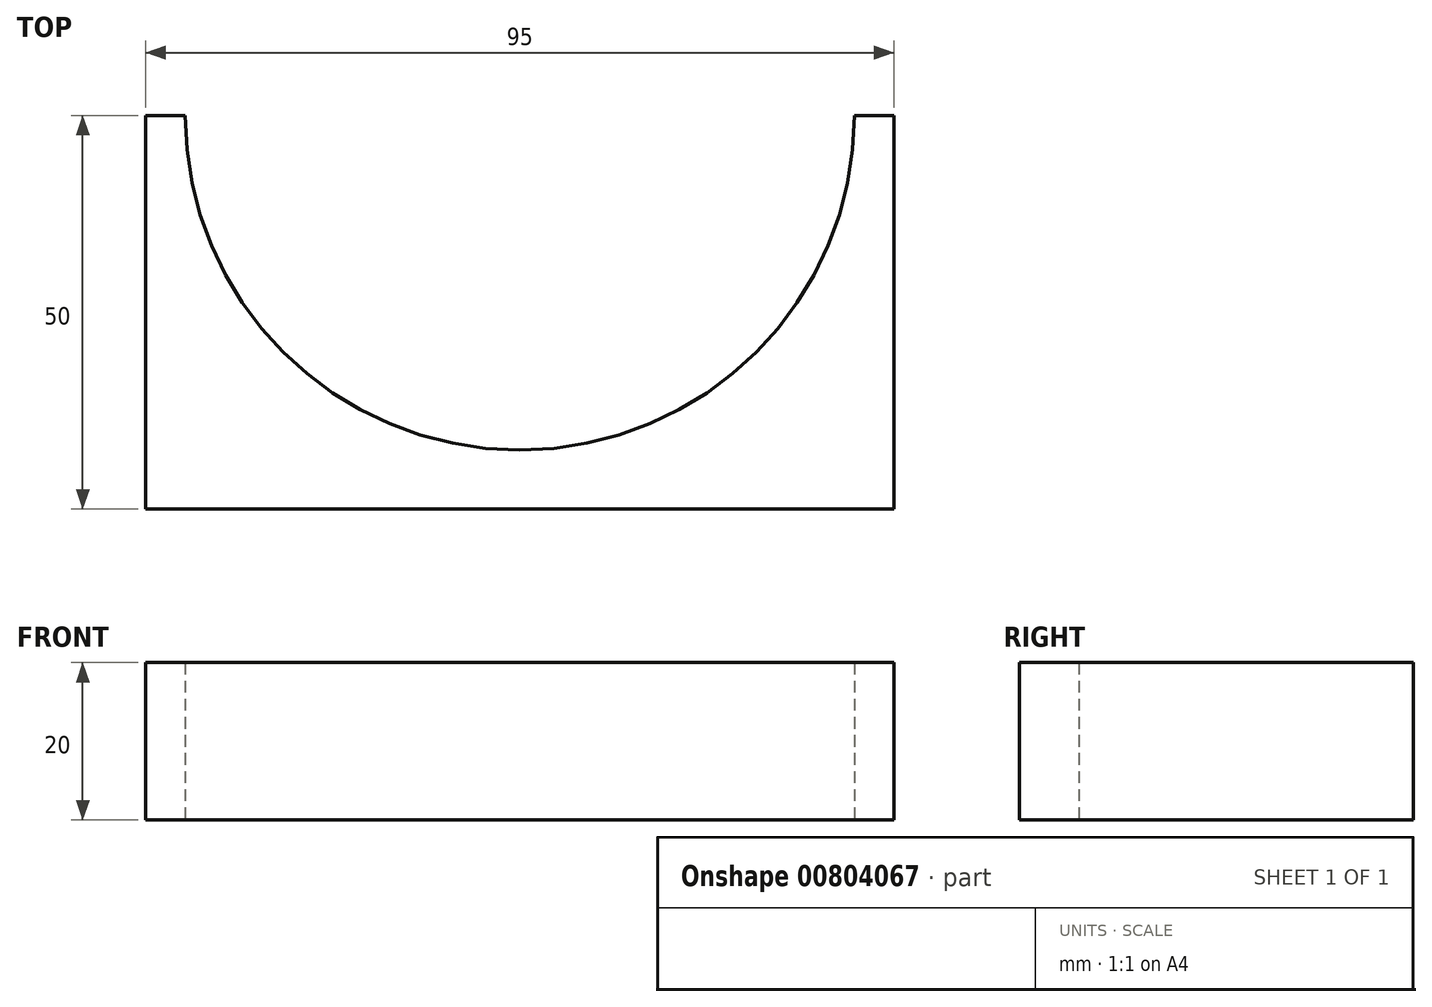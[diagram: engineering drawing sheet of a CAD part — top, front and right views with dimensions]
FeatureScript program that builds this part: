
annotation { "Feature Type Name" : "Feature", "Feature Type Description" : "" }
export const myFeature = defineFeature(function(context is Context, id is Id, definition is map)
    precondition{}
    {
        {
            var Q0;
            Q0=qCreatedBy(makeId("Top.planeOp"),FACE);
            var sketch = newSketch(context, id + "F0", { "sketchPlane" : qUnion([Q0])});
            skArc(sketch, "E0", {"start": v(-42.5, 0) * mm, "mid": v(0, -42.5) * mm, "end": v(42.5, 0) * mm});
            skArc(sketch, "E1", {"start": v(-47.5, 0) * mm, "mid": v(0, -47.5) * mm, "end": v(47.5, 0) * mm});
            skLineSegment(sketch, "E2", {"start": v(-47.5, 0) * mm, "end": v(-42.5, 0) * mm});
            skLineSegment(sketch, "E3.trimOffspring", {"start": v(42.5, 0) * mm, "end": v(47.5, 0) * mm});
            skSolve(sketch);
        }
        {
            var Q0;
            Q0 = qSketchRegion(id + "F0", true);
            extrude(context, id + "F1", {"entities" : qUnion([Q0]), "depth" : 20 * mm, "offsetDistance" : 25 * mm});
        }
        {
            var Q0;
            Q0=makeQuery(id+"F1.opExtrude","CAP_FACE",FACE,{"disambiguationData":[OSD([sQuery(id+"F0.wireOp",EDGE,"E0"),sQuery(id+"F0.wireOp",EDGE,"E1")])],"isStart":false});
            var sketch = newSketch(context, id + "F2", { "sketchPlane" : qUnion([Q0])});
            skLineSegment(sketch, "E4", {"start": v(-47.5, 0) * mm, "end": v(-47.5, -50) * mm});
            skLineSegment(sketch, "E5", {"start": v(47.5, 0) * mm, "end": v(47.5, -50) * mm});
            skLineSegment(sketch, "E6", {"start": v(0, -50) * mm, "end": v(47.5, -50) * mm});
            skLineSegment(sketch, "E7", {"start": v(0, -50) * mm, "end": v(-47.5, -50) * mm});
            skArc(sketch, "E8", {"start": v(-47.5, 0) * mm, "mid": v(0, -47.5) * mm, "end": v(47.5, 0) * mm});
            skLineSegment(sketch, "E9", {"start": v(0, -47.5) * mm, "end": v(0, -50) * mm, "construction": true});
            skSolve(sketch);
        }
        {
            var Q0;
            Q0 = qSketchRegion(id + "F2", true);
            extrude(context, id + "F3", {"entities" : qUnion([Q0]), "operationType" : NewBodyOperationType.ADD, "oppositeDirection" : true, "depth" : 20 * mm, "offsetDistance" : 25 * mm});
        }
    });
